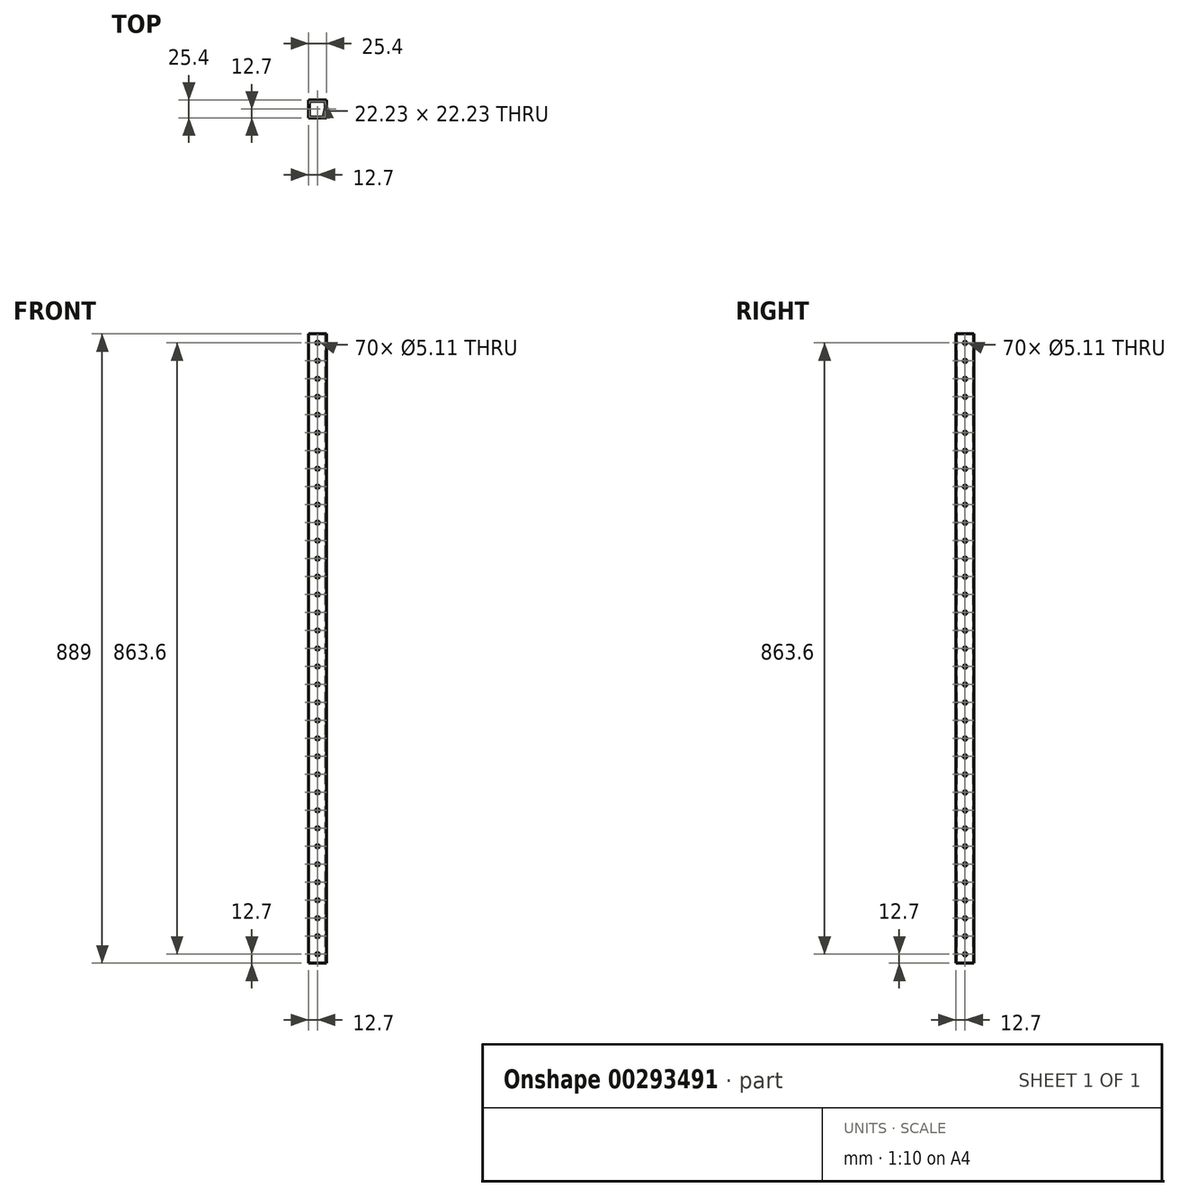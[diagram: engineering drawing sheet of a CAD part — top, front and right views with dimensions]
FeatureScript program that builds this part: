
annotation { "Feature Type Name" : "Feature", "Feature Type Description" : "" }
export const myFeature = defineFeature(function(context is Context, id is Id, definition is map)
    precondition{}
    {
        {
            var Q0;
            Q0=qCreatedBy(makeId("Top.planeOp"),FACE);
            var sketch = newSketch(context, id + "F0", { "sketchPlane" : qUnion([Q0])});
            skLineSegment(sketch, "E0.bottom", {"start": v(12.7, -12.7) * mm, "end": v(-12.7, -12.7) * mm});
            skLineSegment(sketch, "E0.top", {"start": v(12.7, 12.7) * mm, "end": v(-12.7, 12.7) * mm});
            skLineSegment(sketch, "E0.left", {"start": v(12.7, -12.7) * mm, "end": v(12.7, 12.7) * mm});
            skLineSegment(sketch, "E0.right", {"start": v(-12.7, -12.7) * mm, "end": v(-12.7, 12.7) * mm});
            skPoint(sketch, "E0.middle", {"position": v(0, 0) * mm});
            skSolve(sketch);
        }
        {
            var Q0;
            Q0=makeQuery(id+"F0.imprint","IMPRINT",FACE,{"disambiguationData":[TD([[makeQuery(id+"F0.imprint","IMPRINT",EDGE,{"derivedFrom":sQuery(id+"F0.wireOp",EDGE,"E0.bottom")}),-1.0]])]});
            extrude(context, id + "F1", {"entities" : qUnion([Q0]), "depth" : 889 * mm});
        }
        {
            var Q0;
            Q0=makeQuery(id+"F1.opExtrude","CAP_FACE",FACE,{"disambiguationData":[OSD([sQuery(id+"F0.wireOp",EDGE,"E0.bottom"),sQuery(id+"F0.wireOp",EDGE,"E0.top"),sQuery(id+"F0.wireOp",EDGE,"E0.left"),sQuery(id+"F0.wireOp",EDGE,"E0.right")])],"isStart":false});
            var sketch = newSketch(context, id + "F2", { "sketchPlane" : qUnion([Q0])});
            skLineSegment(sketch, "E1.bottom", {"start": v(11.11, -11.11) * mm, "end": v(-11.11, -11.11) * mm});
            skLineSegment(sketch, "E1.top", {"start": v(11.11, 11.11) * mm, "end": v(-11.11, 11.11) * mm});
            skLineSegment(sketch, "E1.left", {"start": v(11.11, -11.11) * mm, "end": v(11.11, 11.11) * mm});
            skLineSegment(sketch, "E1.right", {"start": v(-11.11, -11.11) * mm, "end": v(-11.11, 11.11) * mm});
            skPoint(sketch, "E1.middle", {"position": v(0, 0) * mm});
            skSolve(sketch);
        }
        {
            var Q0;
            Q0=makeQuery(id+"F2.imprint","IMPRINT",FACE,{"disambiguationData":[TD([[makeQuery(id+"F2.imprint","IMPRINT",EDGE,{"derivedFrom":sQuery(id+"F2.wireOp",EDGE,"E1.bottom")}),-1.0]])]});
            extrude(context, id + "F3", {"entities" : qUnion([Q0]), "operationType" : NewBodyOperationType.REMOVE, "oppositeDirection" : true, "depth" : 889 * mm});
        }
        {
            var Q0;
            Q0=makeQuery(id+"F1.opExtrude","SWEPT_FACE",FACE,{"disambiguationData":[OSD([sQuery(id+"F0.wireOp",EDGE,"E0.top")])]});
            var sketch = newSketch(context, id + "F4", { "sketchPlane" : qUnion([Q0])});
            skCircle(sketch, "E2", {"center": v(0, 876.3) * mm, "radius": 2.55 * mm});
            skCircle(sketch, "E3.1.0.0", {"center": v(0, 850.9) * mm, "radius": 2.55 * mm});
            skCircle(sketch, "E3.2.0.0", {"center": v(0, 825.5) * mm, "radius": 2.55 * mm});
            skCircle(sketch, "E3.3.0.0", {"center": v(0, 800.1) * mm, "radius": 2.55 * mm});
            skCircle(sketch, "E3.4.0.0", {"center": v(0, 774.7) * mm, "radius": 2.55 * mm});
            skCircle(sketch, "E3.5.0.0", {"center": v(0, 749.3) * mm, "radius": 2.55 * mm});
            skCircle(sketch, "E3.6.0.0", {"center": v(0, 723.9) * mm, "radius": 2.55 * mm});
            skCircle(sketch, "E3.7.0.0", {"center": v(0, 698.5) * mm, "radius": 2.55 * mm});
            skCircle(sketch, "E3.8.0.0", {"center": v(0, 673.1) * mm, "radius": 2.55 * mm});
            skCircle(sketch, "E3.9.0.0", {"center": v(0, 647.7) * mm, "radius": 2.55 * mm});
            skCircle(sketch, "E3.10.0.0", {"center": v(0, 622.3) * mm, "radius": 2.55 * mm});
            skCircle(sketch, "E3.11.0.0", {"center": v(0, 596.9) * mm, "radius": 2.55 * mm});
            skCircle(sketch, "E3.12.0.0", {"center": v(0, 571.5) * mm, "radius": 2.55 * mm});
            skCircle(sketch, "E3.13.0.0", {"center": v(0, 546.1) * mm, "radius": 2.55 * mm});
            skCircle(sketch, "E3.14.0.0", {"center": v(0, 520.7) * mm, "radius": 2.55 * mm});
            skCircle(sketch, "E3.15.0.0", {"center": v(0, 495.3) * mm, "radius": 2.55 * mm});
            skCircle(sketch, "E3.16.0.0", {"center": v(0, 469.9) * mm, "radius": 2.55 * mm});
            skCircle(sketch, "E3.17.0.0", {"center": v(0, 444.5) * mm, "radius": 2.55 * mm});
            skCircle(sketch, "E3.18.0.0", {"center": v(0, 419.1) * mm, "radius": 2.55 * mm});
            skCircle(sketch, "E3.19.0.0", {"center": v(0, 393.7) * mm, "radius": 2.55 * mm});
            skCircle(sketch, "E3.20.0.0", {"center": v(0, 368.3) * mm, "radius": 2.55 * mm});
            skCircle(sketch, "E3.21.0.0", {"center": v(0, 342.9) * mm, "radius": 2.55 * mm});
            skCircle(sketch, "E3.22.0.0", {"center": v(0, 317.5) * mm, "radius": 2.55 * mm});
            skCircle(sketch, "E3.23.0.0", {"center": v(0, 292.1) * mm, "radius": 2.55 * mm});
            skCircle(sketch, "E3.24.0.0", {"center": v(0, 266.7) * mm, "radius": 2.55 * mm});
            skCircle(sketch, "E3.25.0.0", {"center": v(0, 241.3) * mm, "radius": 2.55 * mm});
            skCircle(sketch, "E3.26.0.0", {"center": v(0, 215.9) * mm, "radius": 2.55 * mm});
            skCircle(sketch, "E3.27.0.0", {"center": v(0, 190.5) * mm, "radius": 2.55 * mm});
            skCircle(sketch, "E3.28.0.0", {"center": v(0, 165.1) * mm, "radius": 2.55 * mm});
            skCircle(sketch, "E3.29.0.0", {"center": v(0, 139.7) * mm, "radius": 2.55 * mm});
            skCircle(sketch, "E3.30.0.0", {"center": v(0, 114.3) * mm, "radius": 2.55 * mm});
            skCircle(sketch, "E3.31.0.0", {"center": v(0, 88.9) * mm, "radius": 2.55 * mm});
            skCircle(sketch, "E3.32.0.0", {"center": v(0, 63.5) * mm, "radius": 2.55 * mm});
            skCircle(sketch, "E3.33.0.0", {"center": v(0, 38.1) * mm, "radius": 2.55 * mm});
            skCircle(sketch, "E3.34.0.0", {"center": v(0, 12.7) * mm, "radius": 2.55 * mm});
            skLineSegment(sketch, "E3.direction1", {"start": v(0, 876.3) * mm, "end": v(0, 850.9) * mm, "construction": true});
            skSolve(sketch);
        }
        {
            var Q0;
            Q0=sQuery(id+"F4.wireOp",VERTEX,"E2.center");
            var Q1;
            Q1=sQuery(id+"F4.wireOp",VERTEX,"E3.1.0.0.center");
            var Q2;
            Q2=sQuery(id+"F4.wireOp",VERTEX,"E3.2.0.0.center");
            var Q3;
            Q3=sQuery(id+"F4.wireOp",VERTEX,"E3.3.0.0.center");
            var Q4;
            Q4=sQuery(id+"F4.wireOp",VERTEX,"E3.4.0.0.center");
            var Q5;
            Q5=sQuery(id+"F4.wireOp",VERTEX,"E3.5.0.0.center");
            var Q6;
            Q6=sQuery(id+"F4.wireOp",VERTEX,"E3.6.0.0.center");
            var Q7;
            Q7=sQuery(id+"F4.wireOp",VERTEX,"E3.7.0.0.center");
            var Q8;
            Q8=sQuery(id+"F4.wireOp",VERTEX,"E3.8.0.0.center");
            var Q9;
            Q9=sQuery(id+"F4.wireOp",VERTEX,"E3.9.0.0.center");
            var Q10;
            Q10=sQuery(id+"F4.wireOp",VERTEX,"E3.10.0.0.center");
            var Q11;
            Q11=sQuery(id+"F4.wireOp",VERTEX,"E3.11.0.0.center");
            var Q12;
            Q12=sQuery(id+"F4.wireOp",VERTEX,"E3.12.0.0.center");
            var Q13;
            Q13=sQuery(id+"F4.wireOp",VERTEX,"E3.13.0.0.center");
            var Q14;
            Q14=sQuery(id+"F4.wireOp",VERTEX,"E3.14.0.0.center");
            var Q15;
            Q15=sQuery(id+"F4.wireOp",VERTEX,"E3.16.0.0.center");
            var Q16;
            Q16=sQuery(id+"F4.wireOp",VERTEX,"E3.17.0.0.center");
            var Q17;
            Q17=sQuery(id+"F4.wireOp",VERTEX,"E3.18.0.0.center");
            var Q18;
            Q18=sQuery(id+"F4.wireOp",VERTEX,"E3.15.0.0.center");
            var Q19;
            Q19=sQuery(id+"F4.wireOp",VERTEX,"E3.19.0.0.center");
            var Q20;
            Q20=sQuery(id+"F4.wireOp",VERTEX,"E3.20.0.0.center");
            var Q21;
            Q21=sQuery(id+"F4.wireOp",VERTEX,"E3.21.0.0.center");
            var Q22;
            Q22=sQuery(id+"F4.wireOp",VERTEX,"E3.22.0.0.center");
            var Q23;
            Q23=sQuery(id+"F4.wireOp",VERTEX,"E3.23.0.0.center");
            var Q24;
            Q24=sQuery(id+"F4.wireOp",VERTEX,"E3.24.0.0.center");
            var Q25;
            Q25=sQuery(id+"F4.wireOp",VERTEX,"E3.25.0.0.center");
            var Q26;
            Q26=sQuery(id+"F4.wireOp",VERTEX,"E3.26.0.0.center");
            var Q27;
            Q27=sQuery(id+"F4.wireOp",VERTEX,"E3.27.0.0.center");
            var Q28;
            Q28=sQuery(id+"F4.wireOp",VERTEX,"E3.28.0.0.center");
            var Q29;
            Q29=sQuery(id+"F4.wireOp",VERTEX,"E3.29.0.0.center");
            var Q30;
            Q30=sQuery(id+"F4.wireOp",VERTEX,"E3.30.0.0.center");
            var Q31;
            Q31=sQuery(id+"F4.wireOp",VERTEX,"E3.31.0.0.center");
            var Q32;
            Q32=sQuery(id+"F4.wireOp",VERTEX,"E3.32.0.0.center");
            var Q33;
            Q33=sQuery(id+"F4.wireOp",VERTEX,"E3.33.0.0.center");
            var Q34;
            Q34=sQuery(id+"F4.wireOp",VERTEX,"E3.34.0.0.center");
            var Q35;
            Q35=makeQuery(id+"F1.opExtrude","SWEPT_BODY",BODY,{"disambiguationData":[OSD([sQuery(id+"F0.wireOp",EDGE,"E0.bottom"),sQuery(id+"F0.wireOp",EDGE,"E0.top"),sQuery(id+"F0.wireOp",EDGE,"E0.left"),sQuery(id+"F0.wireOp",EDGE,"E0.right")])]});
            hole(context, id + "F5", {"style" : HoleStyle.SIMPLE, "endStyle" : HoleEndStyle.THROUGH, "holeDiameter" : 5.1 * mm, "tappedDepth" : 12.7 * mm, "tapClearance" : 3, "locations" : qUnion([Q0, Q1, Q2, Q3, Q4, Q5, Q6, Q7, Q8, Q9, Q10, Q11, Q12, Q13, Q14, Q15, Q16, Q17, Q18, Q19, Q20, Q21, Q22, Q23, Q24, Q25, Q26, Q27, Q28, Q29, Q30, Q31, Q32, Q33, Q34]), "scope" : qUnion([Q35])});
        }
        {
            var Q0;
            Q0=makeQuery(id+"F1.opExtrude","SWEPT_FACE",FACE,{"disambiguationData":[OSD([sQuery(id+"F0.wireOp",EDGE,"E0.left")])]});
            var sketch = newSketch(context, id + "F6", { "sketchPlane" : qUnion([Q0])});
            skCircle(sketch, "E4", {"center": v(0, 876.3) * mm, "radius": 2.55 * mm});
            skCircle(sketch, "E5.0.1.0", {"center": v(0, 850.9) * mm, "radius": 2.55 * mm});
            skCircle(sketch, "E5.0.2.0", {"center": v(0, 825.5) * mm, "radius": 2.55 * mm});
            skCircle(sketch, "E5.0.3.0", {"center": v(0, 800.1) * mm, "radius": 2.55 * mm});
            skCircle(sketch, "E5.0.4.0", {"center": v(0, 774.7) * mm, "radius": 2.55 * mm});
            skCircle(sketch, "E5.0.5.0", {"center": v(0, 749.3) * mm, "radius": 2.55 * mm});
            skCircle(sketch, "E5.0.6.0", {"center": v(0, 723.9) * mm, "radius": 2.55 * mm});
            skCircle(sketch, "E5.0.7.0", {"center": v(0, 698.5) * mm, "radius": 2.55 * mm});
            skCircle(sketch, "E5.0.8.0", {"center": v(0, 673.1) * mm, "radius": 2.55 * mm});
            skCircle(sketch, "E5.0.9.0", {"center": v(0, 647.7) * mm, "radius": 2.55 * mm});
            skCircle(sketch, "E5.0.10.0", {"center": v(0, 622.3) * mm, "radius": 2.55 * mm});
            skCircle(sketch, "E5.0.11.0", {"center": v(0, 596.9) * mm, "radius": 2.55 * mm});
            skCircle(sketch, "E5.0.12.0", {"center": v(0, 571.5) * mm, "radius": 2.55 * mm});
            skCircle(sketch, "E5.0.13.0", {"center": v(0, 546.1) * mm, "radius": 2.55 * mm});
            skCircle(sketch, "E5.0.14.0", {"center": v(0, 520.7) * mm, "radius": 2.55 * mm});
            skCircle(sketch, "E5.0.15.0", {"center": v(0, 495.3) * mm, "radius": 2.55 * mm});
            skCircle(sketch, "E5.0.16.0", {"center": v(0, 469.9) * mm, "radius": 2.55 * mm});
            skCircle(sketch, "E5.0.17.0", {"center": v(0, 444.5) * mm, "radius": 2.55 * mm});
            skCircle(sketch, "E5.0.18.0", {"center": v(0, 419.1) * mm, "radius": 2.55 * mm});
            skCircle(sketch, "E5.0.19.0", {"center": v(0, 393.7) * mm, "radius": 2.55 * mm});
            skCircle(sketch, "E5.0.20.0", {"center": v(0, 368.3) * mm, "radius": 2.55 * mm});
            skCircle(sketch, "E5.0.21.0", {"center": v(0, 342.9) * mm, "radius": 2.55 * mm});
            skCircle(sketch, "E5.0.22.0", {"center": v(0, 317.5) * mm, "radius": 2.55 * mm});
            skCircle(sketch, "E5.0.23.0", {"center": v(0, 292.1) * mm, "radius": 2.55 * mm});
            skCircle(sketch, "E5.0.24.0", {"center": v(0, 266.7) * mm, "radius": 2.55 * mm});
            skCircle(sketch, "E5.0.25.0", {"center": v(0, 241.3) * mm, "radius": 2.55 * mm});
            skCircle(sketch, "E5.0.26.0", {"center": v(0, 215.9) * mm, "radius": 2.55 * mm});
            skCircle(sketch, "E5.0.27.0", {"center": v(0, 190.5) * mm, "radius": 2.55 * mm});
            skCircle(sketch, "E5.0.28.0", {"center": v(0, 165.1) * mm, "radius": 2.55 * mm});
            skCircle(sketch, "E5.0.29.0", {"center": v(0, 139.7) * mm, "radius": 2.55 * mm});
            skCircle(sketch, "E5.0.30.0", {"center": v(0, 114.3) * mm, "radius": 2.55 * mm});
            skCircle(sketch, "E5.0.31.0", {"center": v(0, 88.9) * mm, "radius": 2.55 * mm});
            skCircle(sketch, "E5.0.32.0", {"center": v(0, 63.5) * mm, "radius": 2.55 * mm});
            skCircle(sketch, "E5.0.33.0", {"center": v(0, 38.1) * mm, "radius": 2.55 * mm});
            skCircle(sketch, "E5.0.34.0", {"center": v(0, 12.7) * mm, "radius": 2.55 * mm});
            skLineSegment(sketch, "E5.direction1", {"start": v(0, 876.3) * mm, "end": v(25.4, 876.3) * mm, "construction": true});
            skLineSegment(sketch, "E5.direction2", {"start": v(0, 876.3) * mm, "end": v(0, 850.9) * mm, "construction": true});
            skSolve(sketch);
        }
        {
            var Q0;
            Q0=sQuery(id+"F6.wireOp",VERTEX,"E5.0.33.0.center");
            var Q1;
            Q1=sQuery(id+"F6.wireOp",VERTEX,"E5.0.17.0.center");
            var Q2;
            Q2=sQuery(id+"F6.wireOp",VERTEX,"E5.0.13.0.center");
            var Q3;
            Q3=sQuery(id+"F6.wireOp",VERTEX,"E5.0.29.0.center");
            var Q4;
            Q4=sQuery(id+"F6.wireOp",VERTEX,"E5.0.26.0.center");
            var Q5;
            Q5=sQuery(id+"F6.wireOp",VERTEX,"E5.0.15.0.center");
            var Q6;
            Q6=sQuery(id+"F6.wireOp",VERTEX,"E5.0.31.0.center");
            var Q7;
            Q7=sQuery(id+"F6.wireOp",VERTEX,"E5.0.12.0.center");
            var Q8;
            Q8=sQuery(id+"F6.wireOp",VERTEX,"E5.0.20.0.center");
            var Q9;
            Q9=sQuery(id+"F6.wireOp",VERTEX,"E5.0.10.0.center");
            var Q10;
            Q10=sQuery(id+"F6.wireOp",VERTEX,"E5.0.4.0.center");
            var Q11;
            Q11=sQuery(id+"F6.wireOp",VERTEX,"E5.0.6.0.center");
            var Q12;
            Q12=sQuery(id+"F6.wireOp",VERTEX,"E5.0.24.0.center");
            var Q13;
            Q13=sQuery(id+"F6.wireOp",VERTEX,"E5.direction1.start");
            var Q14;
            Q14=sQuery(id+"F6.wireOp",VERTEX,"E5.0.28.0.center");
            var Q15;
            Q15=sQuery(id+"F6.wireOp",VERTEX,"E5.0.22.0.center");
            var Q16;
            Q16=sQuery(id+"F6.wireOp",VERTEX,"E5.0.1.0.center");
            var Q17;
            Q17=sQuery(id+"F6.wireOp",VERTEX,"E5.0.19.0.center");
            var Q18;
            Q18=sQuery(id+"F6.wireOp",VERTEX,"E5.0.2.0.center");
            var Q19;
            Q19=sQuery(id+"F6.wireOp",VERTEX,"E5.direction1.end");
            var Q20;
            Q20=sQuery(id+"F6.wireOp",VERTEX,"E5.0.8.0.center");
            var Q21;
            Q21=sQuery(id+"F6.wireOp",VERTEX,"E5.0.34.0.center");
            var Q22;
            Q22=sQuery(id+"F6.wireOp",VERTEX,"E5.0.16.0.center");
            var Q23;
            Q23=sQuery(id+"F6.wireOp",VERTEX,"E5.0.32.0.center");
            var Q24;
            Q24=sQuery(id+"F6.wireOp",VERTEX,"E5.0.14.0.center");
            var Q25;
            Q25=sQuery(id+"F6.wireOp",VERTEX,"E5.0.30.0.center");
            var Q26;
            Q26=sQuery(id+"F6.wireOp",VERTEX,"E5.0.9.0.center");
            var Q27;
            Q27=sQuery(id+"F6.wireOp",VERTEX,"E5.0.3.0.center");
            var Q28;
            Q28=sQuery(id+"F6.wireOp",VERTEX,"E5.0.7.0.center");
            var Q29;
            Q29=sQuery(id+"F6.wireOp",VERTEX,"E5.0.11.0.center");
            var Q30;
            Q30=sQuery(id+"F6.wireOp",VERTEX,"E5.0.21.0.center");
            var Q31;
            Q31=sQuery(id+"F6.wireOp",VERTEX,"E5.0.27.0.center");
            var Q32;
            Q32=sQuery(id+"F6.wireOp",VERTEX,"E5.0.25.0.center");
            var Q33;
            Q33=sQuery(id+"F6.wireOp",VERTEX,"E5.0.23.0.center");
            var Q34;
            Q34=sQuery(id+"F6.wireOp",VERTEX,"E5.0.18.0.center");
            var Q35;
            Q35=sQuery(id+"F6.wireOp",VERTEX,"E5.0.5.0.center");
            var Q36;
            Q36=makeQuery(id+"F1.opExtrude","SWEPT_BODY",BODY,{"disambiguationData":[OSD([sQuery(id+"F0.wireOp",EDGE,"E0.bottom"),sQuery(id+"F0.wireOp",EDGE,"E0.top"),sQuery(id+"F0.wireOp",EDGE,"E0.left"),sQuery(id+"F0.wireOp",EDGE,"E0.right")])]});
            hole(context, id + "F7", {"style" : HoleStyle.SIMPLE, "endStyle" : HoleEndStyle.THROUGH, "holeDiameter" : 5.1 * mm, "tappedDepth" : 12.7 * mm, "tapClearance" : 3, "locations" : qUnion([Q0, Q1, Q2, Q3, Q4, Q5, Q6, Q7, Q8, Q9, Q10, Q11, Q12, Q13, Q14, Q15, Q16, Q17, Q18, Q19, Q20, Q21, Q22, Q23, Q24, Q25, Q26, Q27, Q28, Q29, Q30, Q31, Q32, Q33, Q34, Q35]), "scope" : qUnion([Q36])});
        }
    });
